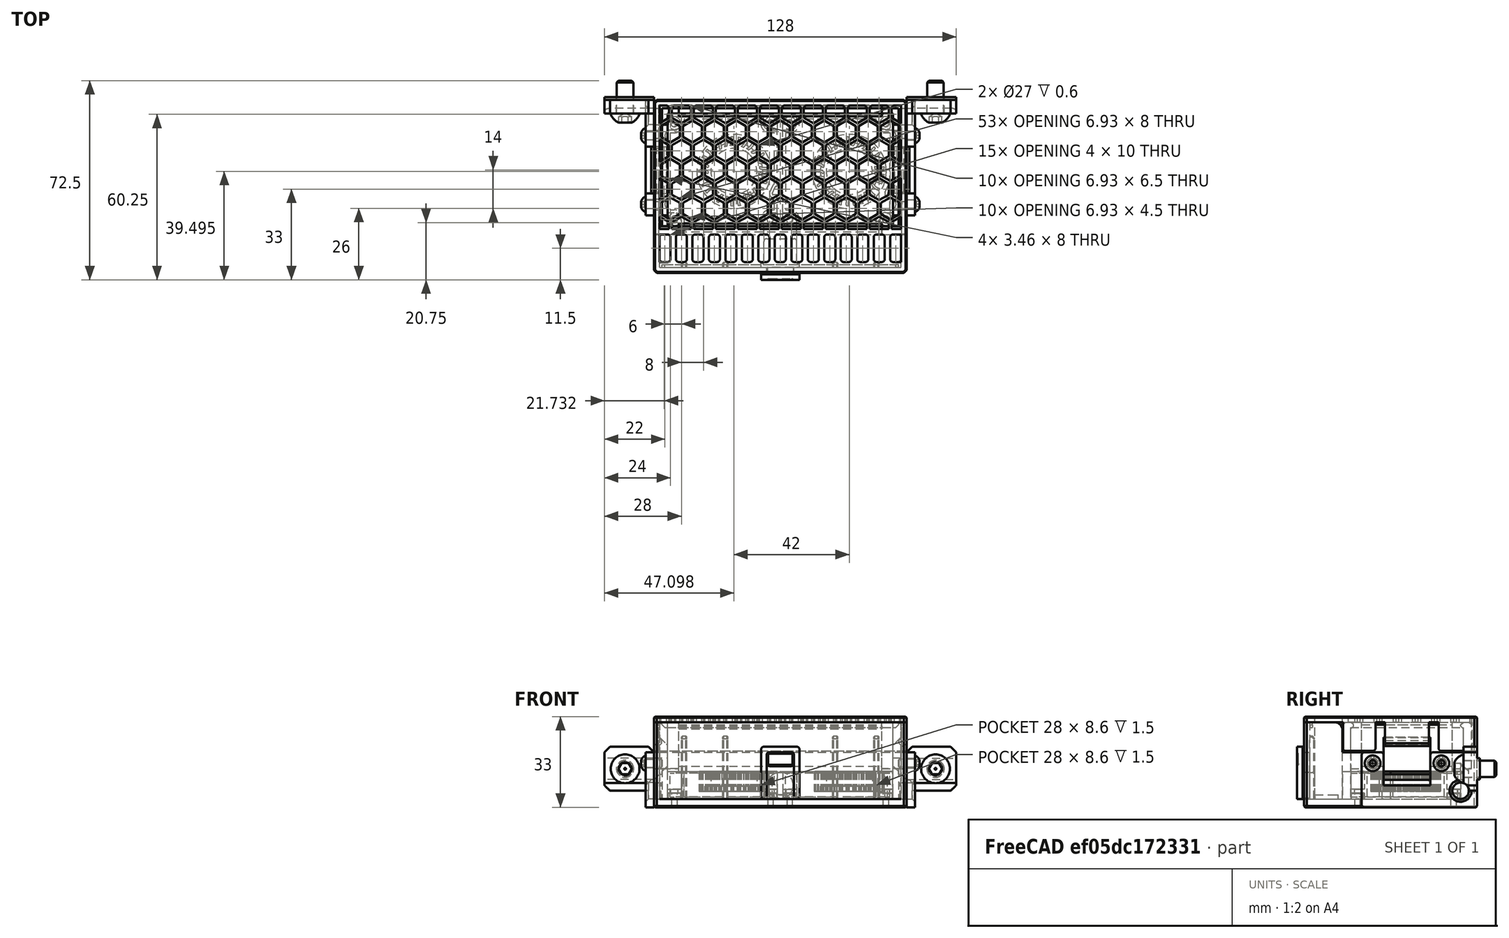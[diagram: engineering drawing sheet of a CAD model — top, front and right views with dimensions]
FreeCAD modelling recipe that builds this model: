
FCSTD DOCUMENT  (FreeCAD 0.19R24291 (Git))
Label: air-filter-assembly
License: Other
LicenseURL: GPL3
objects: Part::Feature×7, Part::FeaturePython×6, Part::Box×2, App::Part×1
note: 15 computed .brp shape members not serialized (recipe doc carries the construction recipe); baked Part::Feature solids carry a one-line shape summary decoded from their .brp

FEATURE [Part::Box] Box  label="hepa-filter"
  AttacherType = Attacher::AttachEngine3D
  Height = 16
  Length = 82
  Placement = pos=(-41,-20.5,13) rot=(0,0,1;0rad)
  Width = 41
FEATURE [Part::Box] Box001  label="active-carbon-foam"
  AttacherType = Attacher::AttachEngine3D
  Height = 28
  Length = 88
  Placement = pos=(-44,-33.5,3) rot=(0,0,1;0rad)
  Width = 10
FEATURE [Part::Feature] Part__Mirroring001001  label="Chamfer010015011016001 (Mirror #1)002"
  shape: bbox 18 x 43 x 22 mm, 33 faces (baked)
FEATURE [Part::Feature] Chamfer010015011016002001
  shape: bbox 18 x 43 x 22 mm, 33 faces (baked)
FEATURE [Part::Feature] Chamfer010015011013001001
  shape: bbox 92 x 63 x 12.5 mm, 653 faces (baked)
FEATURE [Part::Feature] Chamfer010015011010001001
  shape: bbox 92 x 63 x 31 mm, 194 faces (baked)
FEATURE [Part::Feature] Cut019003010005001002001001  label="level002"
  shape: bbox 14 x 15 x 19 mm, 37 faces (baked)
FEATURE [Part::Feature] Fusion036012039009  label="4010-fan001"
  Placement = pos=(-21.1,-20.5,3) rot=(-1,0,0;1.5708rad)
  shape: bbox 40 x 40 x 10 mm, 256 faces, 2 solids (baked)
FEATURE [Part::Feature] Fusion001021004009015013015  label="4010-fan002"
  Placement = pos=(20.9,-20.5,3) rot=(-1,0,0;1.5708rad)
  shape: bbox 40 x 40 x 10 mm, 256 faces, 2 solids (baked)
FEATURE [Part::FeaturePython] Screw  label="M3x6-Screw"  # Fasteners workbench fastener (typed FeaturePython)
  Placement = pos=(-49,12.5,16) rot=(0,-1,0;1.5708rad)
  baseObject = -> Part__Mirroring001001 [Edge89]
  diameter = 1
  invert = true
  length = 0
  lengthCustom = 6
  matchOuter = true
  offset = 0
  thread = false
  type = 39
FEATURE [Part::FeaturePython] Screw001  label="M3x6-Screw004"  # Fasteners workbench fastener (typed FeaturePython)
  Placement = pos=(-49,-12.5,16) rot=(0,-1,0;1.5708rad)
  baseObject = -> Part__Mirroring001001 [Edge91]
  diameter = 1
  invert = true
  length = 0
  lengthCustom = 6
  matchOuter = true
  offset = 0
  thread = false
  type = 39
FEATURE [Part::FeaturePython] Screw002  label="M3x6-Screw002"  # Fasteners workbench fastener (typed FeaturePython)
  Placement = pos=(49,12.5,16) rot=(0,1,0;1.5708rad)
  baseObject = -> Chamfer010015011016002001 [Edge89]
  diameter = 1
  invert = false
  length = 0
  lengthCustom = 6
  matchOuter = true
  offset = 0
  thread = false
  type = 39
FEATURE [Part::FeaturePython] Screw003  label="M3x6-Screw003"  # Fasteners workbench fastener (typed FeaturePython)
  Placement = pos=(49,-12.5,16) rot=(0,1,0;1.5708rad)
  baseObject = -> Chamfer010015011016002001 [Edge91]
  diameter = 1
  invert = false
  length = 0
  lengthCustom = 6
  matchOuter = true
  offset = 0
  thread = false
  type = 39
FEATURE [Part::FeaturePython] Screw004  label="M6x12-Screw"  # Fasteners workbench fastener (typed FeaturePython)
  Placement = pos=(-56.5,20.5,14) rot=(1,0,0;1.5708rad)
  baseObject = -> Part__Mirroring001001 [Edge57]
  diameter = 4
  invert = false
  length = 1
  lengthCustom = 12
  matchOuter = true
  offset = 0
  thread = false
  type = 39
FEATURE [Part::FeaturePython] Screw005  label="M6x12-Screw001"  # Fasteners workbench fastener (typed FeaturePython)
  Placement = pos=(56.5,20.5,14) rot=(1,0,0;1.5708rad)
  baseObject = -> Chamfer010015011016002001 [Edge40]
  diameter = 4
  invert = true
  length = 1
  lengthCustom = 12
  matchOuter = true
  offset = 0
  thread = false
  type = 39
FEATURE [App::Part] Part  label="air-filter"
  Group = -> [Box001,Box,Screw,Screw004,Screw001,Part__Mirroring001001,Screw005,Screw002,Screw003,Chamfer010015011016002001,Chamfer010015011013001001,Chamfer010015011010001001,Cut019003010005001002001001,Fusion036012039009,Fusion001021004009015013015]
  Origin = -> Origin
